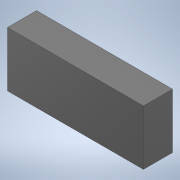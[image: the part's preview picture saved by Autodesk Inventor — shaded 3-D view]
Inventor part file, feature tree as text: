
AUTODESK INVENTOR PART (.ipt)
format: ipt  version: 2021.2 (Build 252289000, 289)  size: 89,088 bytes
history: native  units: in
note: dims shown in document units (in); Inventor stores cm internally (conversion verified against a paired STEP export)
features: extrude x1, sketch x1
ambient origin geometry x8: Origin, YZ Plane, XZ Plane, XY Plane, X Axis, Y Axis, Z Axis, Center Point
bodies: Solid1 (feature_tree)
feature tree (2):
  extrude  "Extrusion1"  Depth=1.74in
  sketch  "Sketch1"  dims[d0=4.3in d1=1.74in d2=0.92in d3=0.0in]
